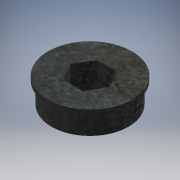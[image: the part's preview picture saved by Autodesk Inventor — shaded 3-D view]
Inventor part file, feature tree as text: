
AUTODESK INVENTOR PART (.ipt)
format: ipt  version: 2016 (Build 200138000, 138)  size: 134,656 bytes
history: native  units: in
note: dims shown in document units (in); Inventor stores cm internally (conversion verified against a paired STEP export)
features: extrude x2, sketch x2
ambient origin geometry x8: Origin, YZ Plane, XZ Plane, XY Plane, X Axis, Y Axis, Z Axis, Center Point
bodies: Solid1 (feature_tree)
feature tree (4):
  extrude  "Extrusion1"  Depth=0.5in
  extrude  "Extrusion2"  Depth=0.06in
  sketch  "Sketch1"  dims[d0=1.125in d1=0.5in]
  sketch  "Sketch2"  dims[d2=0.306in d3=0.0in d4=1.225in d5=0.06in d6=0.0in]
